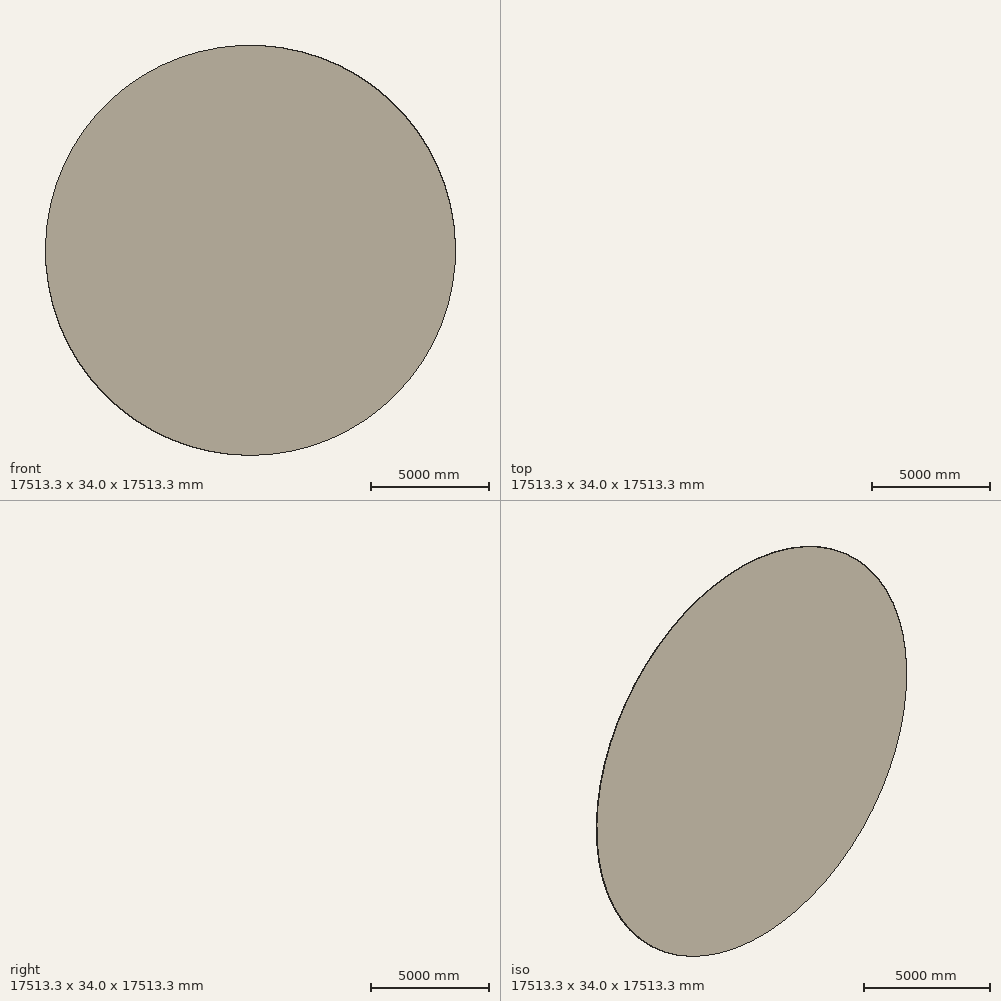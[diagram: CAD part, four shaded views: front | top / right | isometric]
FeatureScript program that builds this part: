
annotation { "Feature Type Name" : "Feature", "Feature Type Description" : "" }
export const myFeature = defineFeature(function(context is Context, id is Id, definition is map)
    precondition{}
    {
        {
            var Q0;
            Q0=qCreatedBy(makeId("Front.planeOp"),FACE);
            var sketch = newSketch(context, id + "F0", { "sketchPlane" : qUnion([Q0])});
            skCircle(sketch, "E0", {"center": v(0, 0) * mm, "radius": 8756.65 * mm});
            skSolve(sketch);
        }
        {
            var Q0;
            Q0=makeQuery(id+"F0.imprint","IMPRINT",FACE,{"disambiguationData":[TD([[makeQuery(id+"F0.imprint","IMPRINT",EDGE,{"derivedFrom":sQuery(id+"F0.wireOp",EDGE,"E0")}),1.0]])]});
            extrude(context, id + "F1", {"entities" : qUnion([Q0]), "depth" : 34 * mm});
        }
    });
